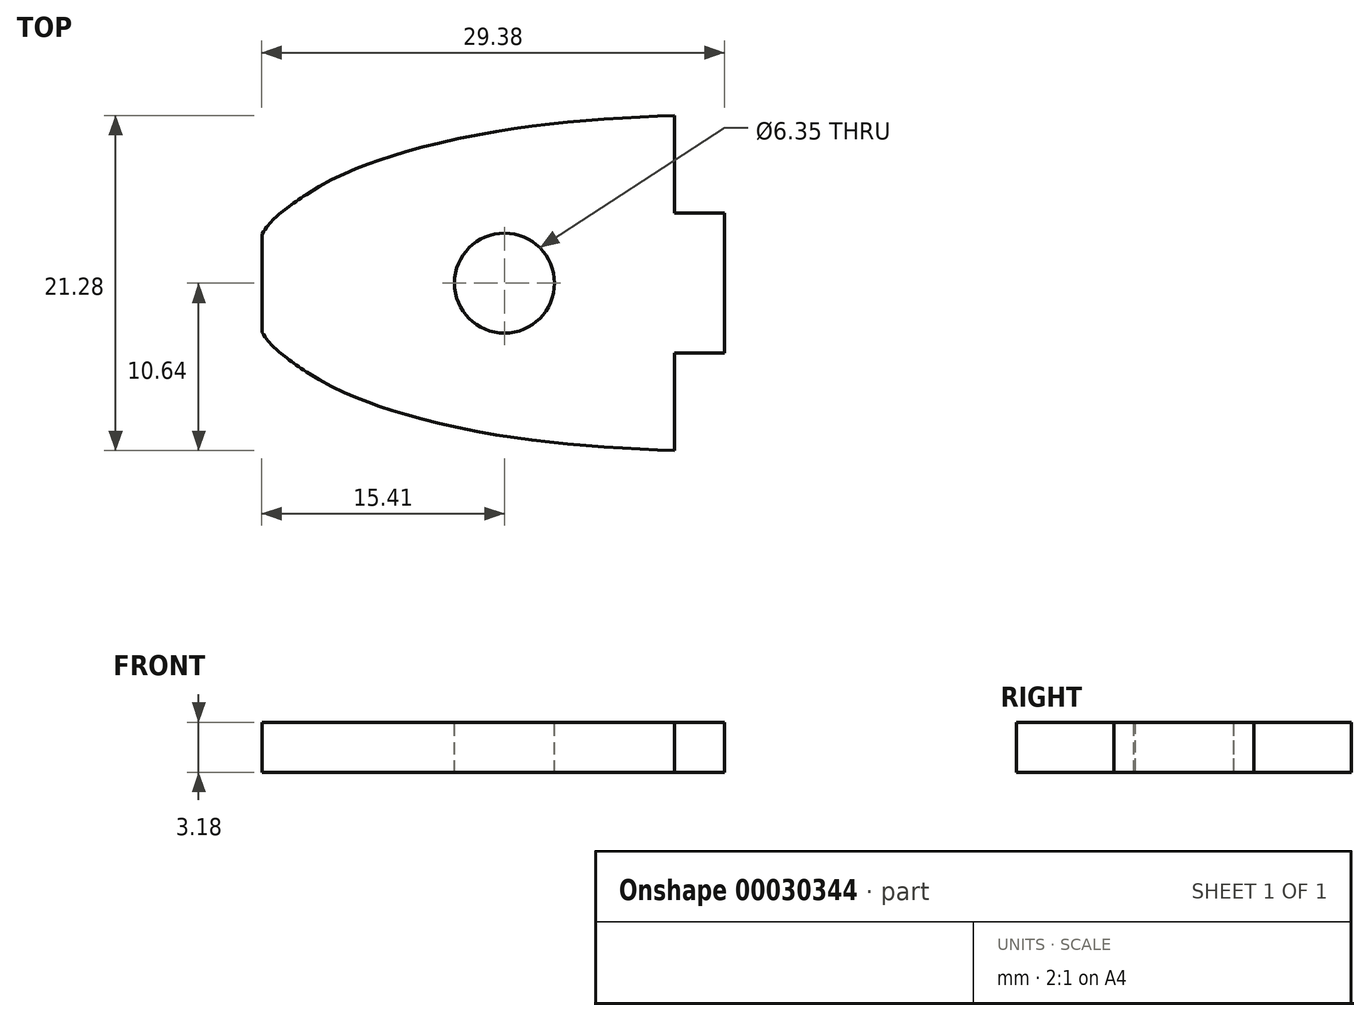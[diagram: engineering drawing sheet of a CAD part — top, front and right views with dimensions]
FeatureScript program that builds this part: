
annotation { "Feature Type Name" : "Feature", "Feature Type Description" : "" }
export const myFeature = defineFeature(function(context is Context, id is Id, definition is map)
    precondition{}
    {
        {
            var Q0;
            Q0=qCreatedBy(makeId("Top.planeOp"),FACE);
            var sketch = newSketch(context, id + "F0", { "sketchPlane" : qUnion([Q0])});
            skFitSpline(sketch, "E0", {"points": [v(101.6, 0.22) * mm, v(96.52, 1.43) * mm, v(91.44, 2.57) * mm, v(81.28, 4.66) * mm, v(71.12, 6.51) * mm, v(60.96, 8.11) * mm, v(50.8, 9.41) * mm, v(40.64, 10.32) * mm, v(30.48, 10.67) * mm, v(25.4, 10.56) * mm, v(20.32, 10.2) * mm, v(15.24, 9.5) * mm, v(10.16, 8.33) * mm, v(7.62, 7.47) * mm, v(5.08, 6.32) * mm, v(2.54, 4.65) * mm, v(1.27, 3.37) * mm, v(0, 0) * mm, v(1.27, -3.37) * mm, v(2.54, -4.65) * mm, v(5.08, -6.32) * mm, v(7.62, -7.47) * mm, v(10.16, -8.33) * mm, v(15.24, -9.5) * mm, v(20.32, -10.2) * mm, v(25.4, -10.56) * mm, v(30.48, -10.67) * mm, v(40.64, -10.32) * mm, v(50.8, -9.41) * mm, v(60.96, -8.11) * mm, v(71.12, -6.51) * mm, v(81.28, -4.66) * mm, v(91.44, -2.57) * mm, v(96.52, -1.43) * mm, v(101.6, -0.22) * mm], "startDerivative": vector(-548.74, 130.7) * mm, "endDerivative": vector(548.74, 130.7) * mm});
            skLineSegment(sketch, "E1", {"start": v(101.6, 0.22) * mm, "end": v(101.6, -0.22) * mm, "construction": true});
            skArc(sketch, "E2", {"start": v(3.94, -4.84) * mm, "mid": v(9.87, 0) * mm, "end": v(3.94, 4.84) * mm});
            skLineSegment(sketch, "E3", {"start": v(27.3, 10.64) * mm, "end": v(27.3, 4.45) * mm});
            skLineSegment(sketch, "E4", {"start": v(27.3, 4.45) * mm, "end": v(30.48, 4.45) * mm});
            skLineSegment(sketch, "E5", {"start": v(30.48, 4.45) * mm, "end": v(30.48, -4.45) * mm});
            skLineSegment(sketch, "E6", {"start": v(30.48, -4.45) * mm, "end": v(27.3, -4.45) * mm});
            skLineSegment(sketch, "E7", {"start": v(27.3, -4.45) * mm, "end": v(27.3, -10.64) * mm});
            skLineSegment(sketch, "E8", {"start": v(3.94, 5.63) * mm, "end": v(3.94, 4.84) * mm});
            skLineSegment(sketch, "E9", {"start": v(3.94, -4.84) * mm, "end": v(3.94, -5.63) * mm});
            skArc(sketch, "E10.trimOffspring", {"start": v(1.1, 3.13) * mm, "mid": v(-0.01, 0) * mm, "end": v(1.1, -3.13) * mm});
            skSolve(sketch);
        }
        {
            var Q0;
            Q0 = qSketchRegion(id + "F0", true);
            extrude(context, id + "F1", {"entities" : qUnion([Q0]), "depth" : 3.17 * mm});
        }
        {
            var Q0;
            Q0=makeQuery(id+"F1.opExtrude","CAP_FACE",FACE,{"disambiguationData":[OSD([sQuery(id+"F0.wireOp",EDGE,"E0"),sQuery(id+"F0.wireOp",EDGE,"E2"),sQuery(id+"F0.wireOp",EDGE,"E3"),sQuery(id+"F0.wireOp",EDGE,"E4"),sQuery(id+"F0.wireOp",EDGE,"E5"),sQuery(id+"F0.wireOp",EDGE,"E6"),sQuery(id+"F0.wireOp",EDGE,"E7"),sQuery(id+"F0.wireOp",EDGE,"E8"),sQuery(id+"F0.wireOp",EDGE,"E9"),sQuery(id+"F0.wireOp",EDGE,"E0")])],"isStart":false});
            var sketch = newSketch(context, id + "F2", { "sketchPlane" : qUnion([Q0])});
            skCircle(sketch, "E11", {"center": v(16.51, 0) * mm, "radius": 3.18 * mm});
            skSolve(sketch);
        }
        {
            var Q0;
            Q0 = qSketchRegion(id + "F2", true);
            extrude(context, id + "F3", {"entities" : qUnion([Q0]), "operationType" : NewBodyOperationType.REMOVE, "endBound" : BoundingType.UP_TO_NEXT, "oppositeDirection" : true, "depth" : 25.4 * mm});
        }
        {
            var Q0;
            Q0=qCreatedBy(makeId("Top.planeOp"),FACE);
            var sketch = newSketch(context, id + "F4", { "sketchPlane" : qUnion([Q0])});
            skLineSegment(sketch, "E12.bottom", {"start": v(-0.17, 3.13) * mm, "end": v(1.1, 3.13) * mm});
            skLineSegment(sketch, "E12.top", {"start": v(-0.17, -3.13) * mm, "end": v(1.1, -3.13) * mm});
            skLineSegment(sketch, "E12.left", {"start": v(-0.17, 3.13) * mm, "end": v(-0.17, -3.13) * mm});
            skLineSegment(sketch, "E12.right", {"start": v(1.1, 3.13) * mm, "end": v(1.1, -3.13) * mm});
            skSolve(sketch);
        }
        {
            var Q0;
            Q0 = qSketchRegion(id + "F4", true);
            extrude(context, id + "F5", {"entities" : qUnion([Q0]), "operationType" : NewBodyOperationType.REMOVE, "depth" : 25.4 * mm, "hasSecondDirection" : true, "secondDirectionOppositeDirection" : true, "secondDirectionDepth" : 25.4 * mm});
        }
    });
